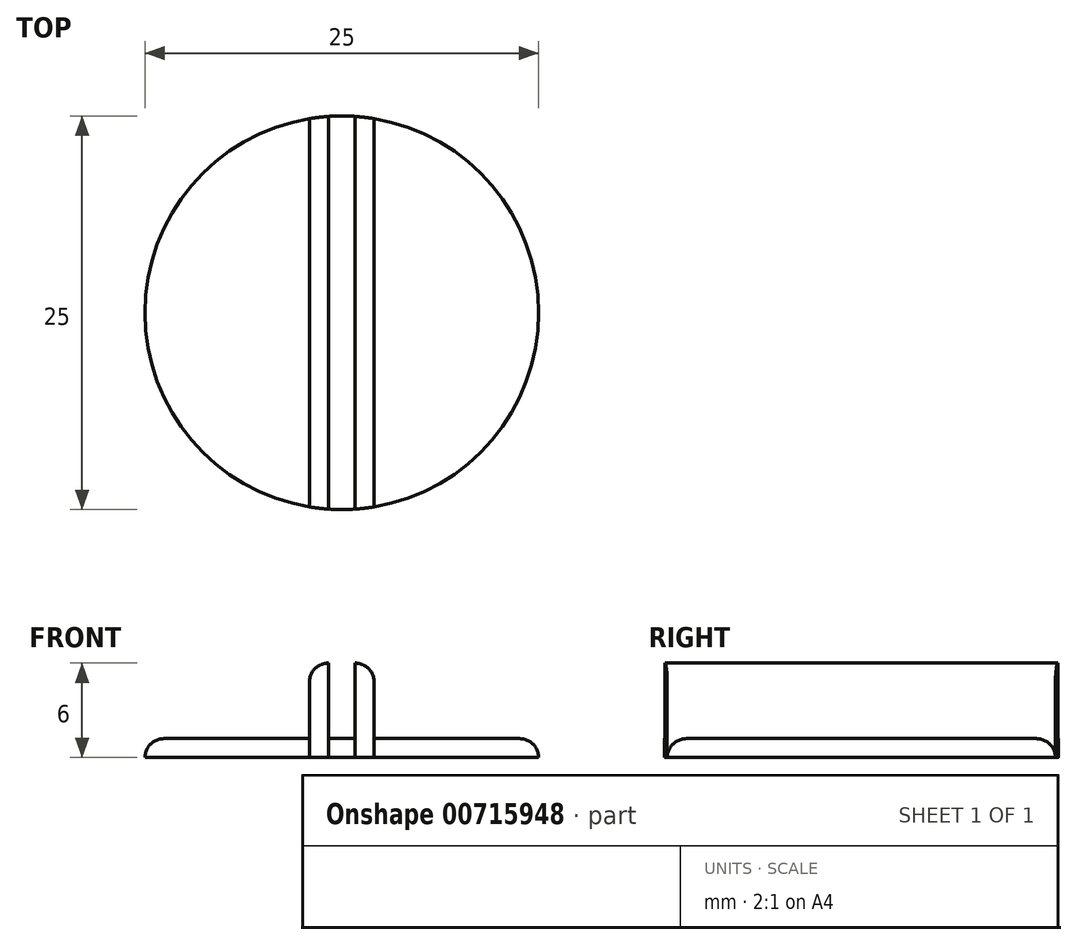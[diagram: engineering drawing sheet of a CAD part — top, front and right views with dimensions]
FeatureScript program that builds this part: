
annotation { "Feature Type Name" : "Feature", "Feature Type Description" : "" }
export const myFeature = defineFeature(function(context is Context, id is Id, definition is map)
    precondition{}
    {
        {
            var Q0;
            Q0=qCreatedBy(makeId("Top.planeOp"),FACE);
            var sketch = newSketch(context, id + "F0", { "sketchPlane" : qUnion([Q0])});
            skCircle(sketch, "E0", {"center": v(0, 0) * mm, "radius": 12.5 * mm});
            skLineSegment(sketch, "E1", {"start": v(0.85, 12.47) * mm, "end": v(0.85, -12.47) * mm});
            skLineSegment(sketch, "E2", {"start": v(-0.85, 12.47) * mm, "end": v(-0.85, -12.47) * mm});
            skLineSegment(sketch, "E3", {"start": v(2.05, 12.33) * mm, "end": v(2.05, -12.33) * mm});
            skLineSegment(sketch, "E4", {"start": v(-2.05, 12.33) * mm, "end": v(-2.05, -12.33) * mm});
            skSolve(sketch);
        }
        {
            var Q0;
            {var subQ0=sQuery(id+"F0.wireOp",EDGE,"E4");Q0=makeQuery(id+"F0.imprint","IMPRINT",FACE,{"disambiguationData":[TD([[makeQuery(id+"F0.imprint","IMPRINT",EDGE,{"derivedFrom":subQ0}),-1.0]])]});}
            var Q1;
            {var subQ0=sQuery(id+"F0.wireOp",EDGE,"E1");Q1=makeQuery(id+"F0.imprint","IMPRINT",FACE,{"disambiguationData":[TD([[makeQuery(id+"F0.imprint","IMPRINT",EDGE,{"derivedFrom":subQ0}),-1.0]])]});}
            var Q2;
            {var subQ0=sQuery(id+"F0.wireOp",EDGE,"E3");Q2=makeQuery(id+"F0.imprint","IMPRINT",FACE,{"disambiguationData":[TD([[makeQuery(id+"F0.imprint","IMPRINT",EDGE,{"derivedFrom":subQ0}),1.0]])]});}
            extrude(context, id + "F1", {"entities" : qUnion([Q0, Q1, Q2]), "depth" : 1.2 * mm, "offsetDistance" : 25 * mm});
        }
        {
            var Q0;
            {var subQ0=sQuery(id+"F0.wireOp",EDGE,"E1");Q0=makeQuery(id+"F0.imprint","IMPRINT",FACE,{"disambiguationData":[TD([[makeQuery(id+"F0.imprint","IMPRINT",EDGE,{"derivedFrom":subQ0}),1.0]])]});}
            var Q1;
            {var subQ0=sQuery(id+"F0.wireOp",EDGE,"E2");Q1=makeQuery(id+"F0.imprint","IMPRINT",FACE,{"disambiguationData":[TD([[makeQuery(id+"F0.imprint","IMPRINT",EDGE,{"derivedFrom":subQ0}),-1.0]])]});}
            extrude(context, id + "F2", {"entities" : qUnion([Q0, Q1]), "depth" : 6 * mm, "offsetDistance" : 25 * mm});
        }
        {
            var Q0;
            {var subQ0=sQuery(id+"F0.wireOp",EDGE,"E4");var subQ1=sQuery(id+"F0.wireOp",EDGE,"E0");Q0=makeQuery(id+"F1.opExtrude","CAP_EDGE",EDGE,{"disambiguationData":[OSD([subQ1]),TDD([makeQuery(id+"F0.imprint","IMPRINT",EDGE,{"disambiguationData":[TD([[makeQuery(id+"F0.imprint","INTERSECT",VERTEX,{"disambiguationData":[OD(0.0)],"derivedFrom":[subQ1,subQ0]}),-1.0]])],"derivedFrom":subQ1})])],"isStart":false});}
            var Q1;
            {var subQ0=sQuery(id+"F0.wireOp",EDGE,"E3");var subQ1=sQuery(id+"F0.wireOp",EDGE,"E0");Q1=makeQuery(id+"F1.opExtrude","CAP_EDGE",EDGE,{"disambiguationData":[OSD([subQ1]),TDD([makeQuery(id+"F0.imprint","IMPRINT",EDGE,{"disambiguationData":[TD([[makeQuery(id+"F0.imprint","INTERSECT",VERTEX,{"disambiguationData":[OD(0.0)],"derivedFrom":[subQ1,subQ0]}),1.0]])],"derivedFrom":subQ1})])],"isStart":false});}
            var Q2;
            Q2=makeQuery(id+"F2.opExtrude","CAP_EDGE",EDGE,{"disambiguationData":[OSD([sQuery(id+"F0.wireOp",EDGE,"E3")])],"isStart":false});
            var Q3;
            Q3=makeQuery(id+"F2.opExtrude","CAP_EDGE",EDGE,{"disambiguationData":[OSD([sQuery(id+"F0.wireOp",EDGE,"E4")])],"isStart":false});
            fillet(context, id + "F3", {"entities" : qUnion([Q0, Q1, Q2, Q3]), "radius" : 1.2 * mm, "tangentPropagation" : true, "allowEdgeOverflow" : false});
        }
    });
